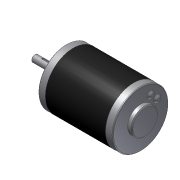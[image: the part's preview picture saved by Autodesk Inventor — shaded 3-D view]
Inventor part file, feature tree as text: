
AUTODESK INVENTOR PART (.ipt)
format: ipt  version: 2012 (Build 160160000, 160)  size: 145,920 bytes
history: native  units: in
note: dims shown in document units (in); Inventor stores cm internally (conversion verified against a paired STEP export)
features: chamfer x1, imported_body x1
ambient origin geometry x8: Origin, YZ Plane, XZ Plane, XY Plane, X Axis, Y Axis, Z Axis, Center Point
feature tree (2):
  chamfer  "Chamfer3"  [1 undecoded]
  imported_body  "Base1"
note: 1 required parameter value undecoded (feature->parameter linkage not recoverable at this tier; creation-order binding heuristic only, values carry confidence <= 0.55)
